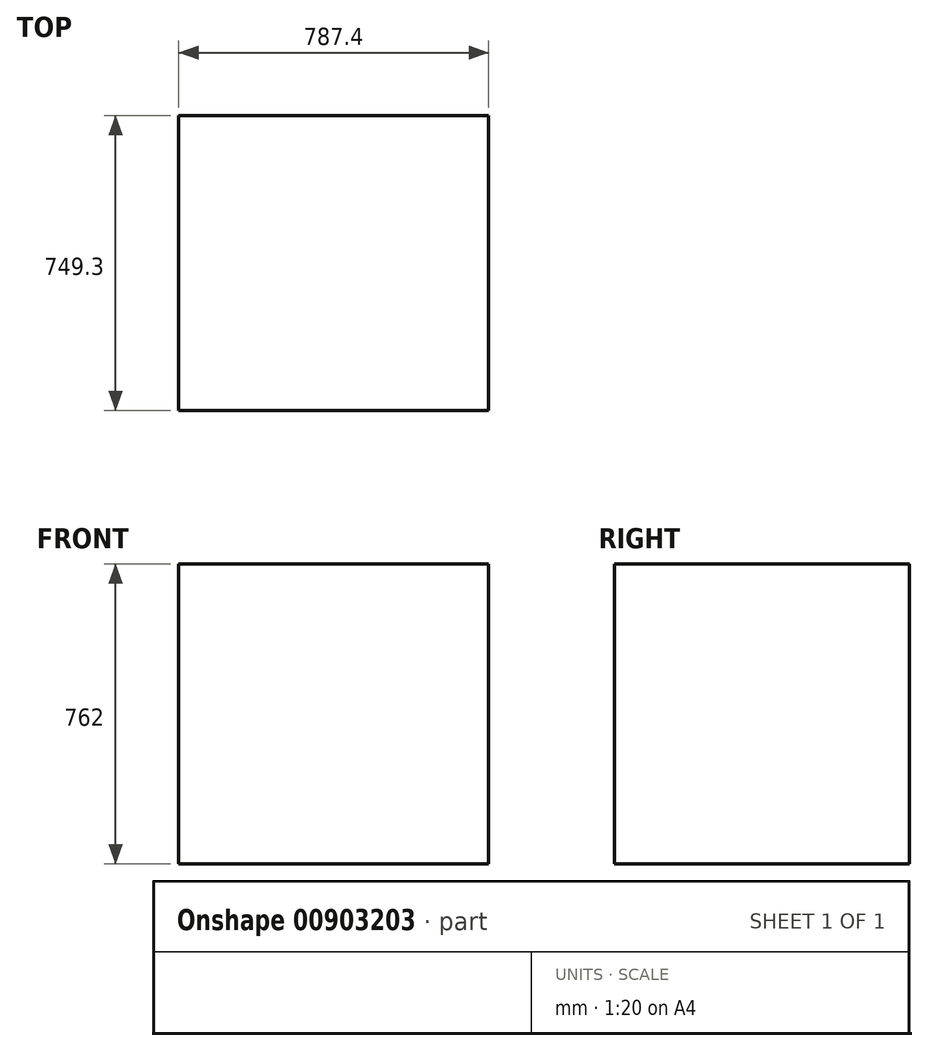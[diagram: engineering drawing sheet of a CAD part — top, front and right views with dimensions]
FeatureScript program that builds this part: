
annotation { "Feature Type Name" : "Feature", "Feature Type Description" : "" }
export const myFeature = defineFeature(function(context is Context, id is Id, definition is map)
    precondition{}
    {
        {
            var Q0;
            Q0=qCreatedBy(makeId("Top.planeOp"),FACE);
            var sketch = newSketch(context, id + "F0", { "sketchPlane" : qUnion([Q0])});
            skLineSegment(sketch, "E0.bottom", {"start": v(393.7, 374.65) * mm, "end": v(-393.7, 374.65) * mm});
            skLineSegment(sketch, "E0.top", {"start": v(393.7, -374.65) * mm, "end": v(-393.7, -374.65) * mm});
            skLineSegment(sketch, "E0.left", {"start": v(393.7, 374.65) * mm, "end": v(393.7, -374.65) * mm});
            skLineSegment(sketch, "E0.right", {"start": v(-393.7, 374.65) * mm, "end": v(-393.7, -374.65) * mm});
            skPoint(sketch, "E0.middle", {"position": v(0, 0) * mm});
            skSolve(sketch);
        }
        {
            var Q0;
            Q0 = qSketchRegion(id + "F0", true);
            extrude(context, id + "F1", {"entities" : qUnion([Q0]), "depth" : 762 * mm, "offsetDistance" : 25.4 * mm});
        }
    });
